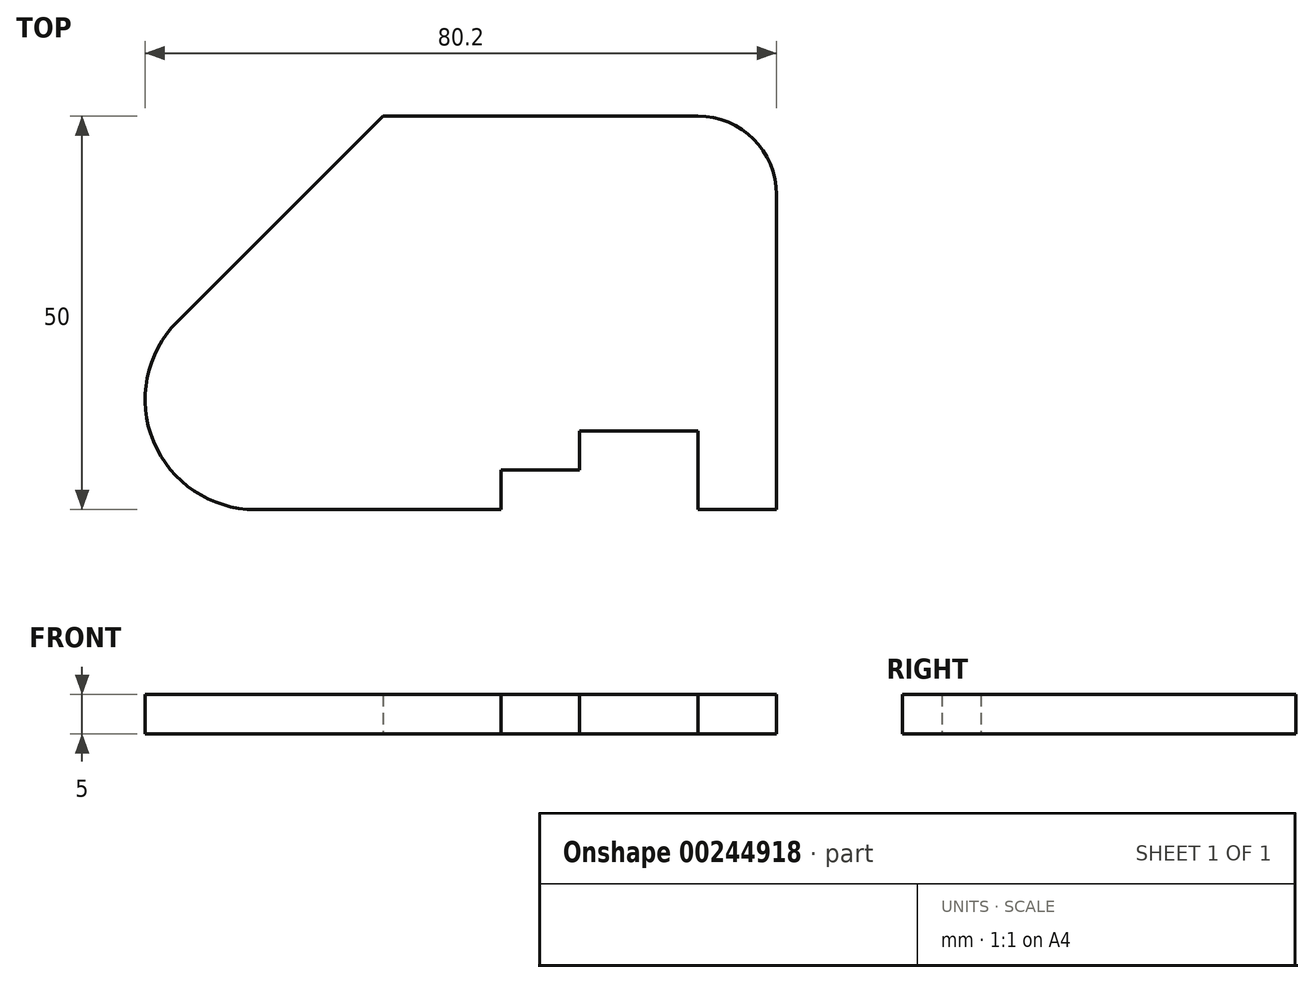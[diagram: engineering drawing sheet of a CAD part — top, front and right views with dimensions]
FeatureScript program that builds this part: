
annotation { "Feature Type Name" : "Feature", "Feature Type Description" : "" }
export const myFeature = defineFeature(function(context is Context, id is Id, definition is map)
    precondition{}
    {
        {
            var Q0;
            Q0=qCreatedBy(makeId("Top.planeOp"),FACE);
            var sketch = newSketch(context, id + "F0", { "sketchPlane" : qUnion([Q0])});
            skLineSegment(sketch, "E0", {"start": v(0, 0) * mm, "end": v(0, 40) * mm});
            skLineSegment(sketch, "E1", {"start": v(0, 40) * mm, "end": v(0, 0) * mm});
            skLineSegment(sketch, "E2", {"start": v(0, 0) * mm, "end": v(-10, 0) * mm});
            skLineSegment(sketch, "E3", {"start": v(-10, 0) * mm, "end": v(-10, 10) * mm});
            skLineSegment(sketch, "E4", {"start": v(-10, 10) * mm, "end": v(-25, 10) * mm});
            skLineSegment(sketch, "E5", {"start": v(-25, 10) * mm, "end": v(-25, 5) * mm});
            skLineSegment(sketch, "E6", {"start": v(-25, 5) * mm, "end": v(-35, 5) * mm});
            skLineSegment(sketch, "E7", {"start": v(-35, 5) * mm, "end": v(-35, 0) * mm});
            skLineSegment(sketch, "E8", {"start": v(-35, 0) * mm, "end": v(-66.2, 0) * mm});
            skLineSegment(sketch, "E9", {"start": v(-10, 50) * mm, "end": v(-50, 50) * mm});
            skLineSegment(sketch, "E10", {"start": v(-50, 50) * mm, "end": v(-76.1, 23.9) * mm});
            skArc(sketch, "E11", {"start": v(-76.1, 23.9) * mm, "mid": v(-79.14, 8.64) * mm, "end": v(-66.2, 0) * mm});
            skArc(sketch, "E12", {"start": v(0, 40) * mm, "mid": v(-2.93, 47.07) * mm, "end": v(-10, 50) * mm});
            skSolve(sketch);
        }
        {
            var Q0;
            Q0 = qSketchRegion(id + "F0", true);
            extrude(context, id + "F1", {"entities" : qUnion([Q0]), "depth" : 5 * mm});
        }
    });
